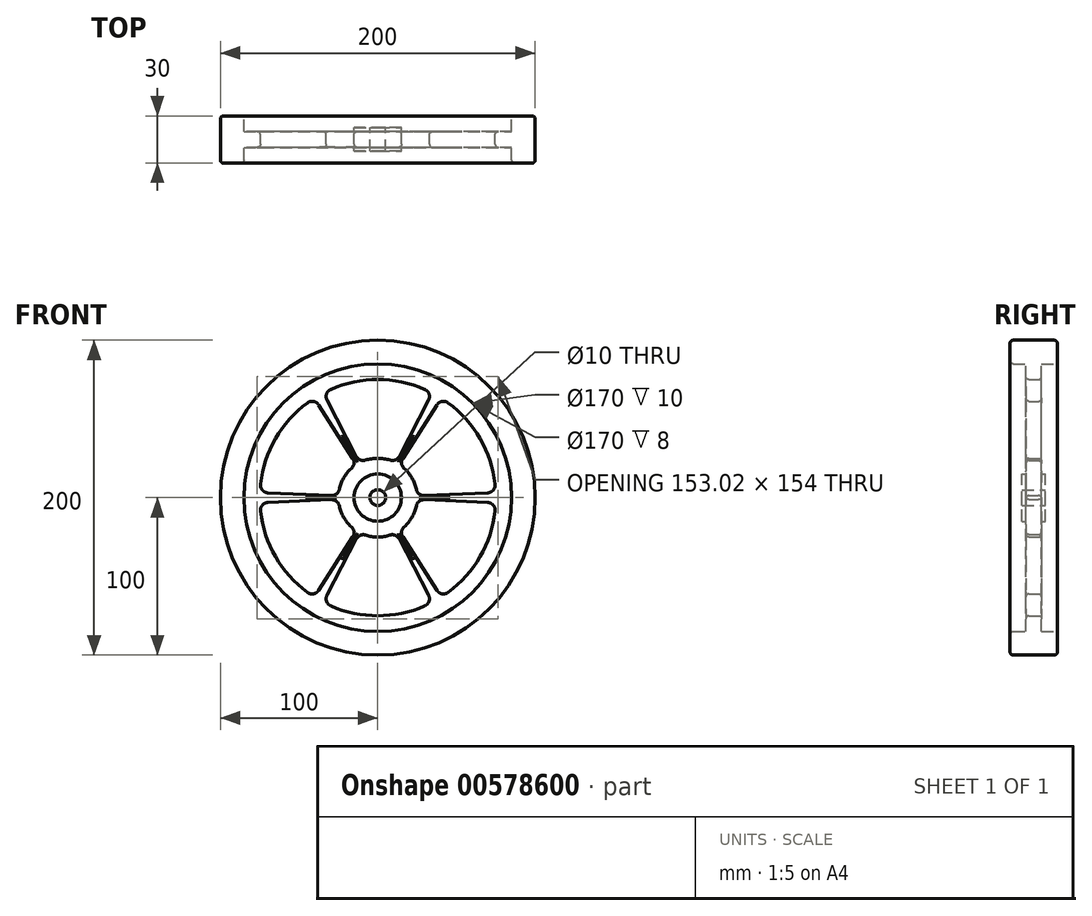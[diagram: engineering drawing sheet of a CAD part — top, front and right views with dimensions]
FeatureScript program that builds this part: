
annotation { "Feature Type Name" : "Feature", "Feature Type Description" : "" }
export const myFeature = defineFeature(function(context is Context, id is Id, definition is map)
    precondition{}
    {
        {
            var Q0;
            Q0=qCreatedBy(makeId("Front.planeOp"),FACE);
            var sketch = newSketch(context, id + "F0", { "sketchPlane" : qUnion([Q0])});
            skCircle(sketch, "E0", {"center": v(0, 0) * mm, "radius": 100 * mm});
            skCircle(sketch, "E1.0", {"center": v(0, 0) * mm, "radius": 85 * mm});
            skCircle(sketch, "E2", {"center": v(0, 0) * mm, "radius": 5 * mm});
            skCircle(sketch, "E3.0", {"center": v(0, 0) * mm, "radius": 15 * mm});
            skArc(sketch, "E4.0", {"start": v(-7.69, -23.79) * mm, "mid": v(0, -25) * mm, "end": v(7.69, -23.79) * mm});
            skArc(sketch, "E5.0", {"start": v(-29.8, -68.83) * mm, "mid": v(0, -75) * mm, "end": v(29.8, -68.83) * mm});
            skLineSegment(sketch, "E6", {"start": v(0, 0) * mm, "end": v(0, -117.3) * mm, "construction": true});
            skLineSegment(sketch, "E7", {"start": v(13.66, -26.24) * mm, "end": v(32.24, -61.93) * mm});
            skLineSegment(sketch, "E8.MirrorCS", {"start": v(-13.66, -26.24) * mm, "end": v(-32.24, -61.93) * mm});
            skPoint(sketch, "E9.visualSharp", {"position": v(34.63, -66.53) * mm});
            skArc(sketch, "E9.filletArc", {"start": v(29.8, -68.83) * mm, "mid": v(32.52, -65.91) * mm, "end": v(32.24, -61.93) * mm});
            skPoint(sketch, "E10.visualSharp", {"position": v(-34.63, -66.53) * mm});
            skArc(sketch, "E10.filletArc", {"start": v(-32.24, -61.93) * mm, "mid": v(-32.52, -65.91) * mm, "end": v(-29.8, -68.83) * mm});
            skPoint(sketch, "E11.visualSharp", {"position": v(-11.54, -22.18) * mm});
            skArc(sketch, "E11.filletArc", {"start": v(-7.69, -23.79) * mm, "mid": v(-11.12, -23.92) * mm, "end": v(-13.66, -26.24) * mm});
            skPoint(sketch, "E12.visualSharp", {"position": v(11.54, -22.18) * mm});
            skArc(sketch, "E12.filletArc", {"start": v(13.66, -26.24) * mm, "mid": v(11.12, -23.92) * mm, "end": v(7.69, -23.79) * mm});
            skLineSegment(sketch, "E13.1.0", {"start": v(29.55, -1.3) * mm, "end": v(69.75, -3.05) * mm});
            skArc(sketch, "E13.1.1", {"start": v(16.76, -18.55) * mm, "mid": v(21.65, -12.5) * mm, "end": v(24.45, -5.24) * mm});
            skArc(sketch, "E13.1.2", {"start": v(16.76, -18.55) * mm, "mid": v(15.16, -21.6) * mm, "end": v(15.9, -24.95) * mm});
            skLineSegment(sketch, "E13.1.3", {"start": v(15.9, -24.95) * mm, "end": v(37.51, -58.89) * mm});
            skArc(sketch, "E13.1.4", {"start": v(29.55, -1.3) * mm, "mid": v(26.28, -2.33) * mm, "end": v(24.45, -5.24) * mm});
            skArc(sketch, "E13.1.5", {"start": v(44.71, -60.21) * mm, "mid": v(64.95, -37.5) * mm, "end": v(74.5, -8.62) * mm});
            skArc(sketch, "E13.1.6", {"start": v(74.5, -8.62) * mm, "mid": v(73.34, -4.8) * mm, "end": v(69.75, -3.05) * mm});
            skArc(sketch, "E13.1.7", {"start": v(37.51, -58.89) * mm, "mid": v(40.82, -61.12) * mm, "end": v(44.71, -60.21) * mm});
            skLineSegment(sketch, "E13.2.0", {"start": v(15.9, 24.95) * mm, "end": v(37.51, 58.89) * mm});
            skArc(sketch, "E13.2.1", {"start": v(24.45, 5.24) * mm, "mid": v(21.65, 12.5) * mm, "end": v(16.76, 18.55) * mm});
            skArc(sketch, "E13.2.2", {"start": v(24.45, 5.24) * mm, "mid": v(26.28, 2.33) * mm, "end": v(29.55, 1.3) * mm});
            skLineSegment(sketch, "E13.2.3", {"start": v(29.55, 1.3) * mm, "end": v(69.75, 3.05) * mm});
            skArc(sketch, "E13.2.4", {"start": v(15.9, 24.95) * mm, "mid": v(15.16, 21.6) * mm, "end": v(16.76, 18.55) * mm});
            skArc(sketch, "E13.2.5", {"start": v(74.5, 8.62) * mm, "mid": v(64.95, 37.5) * mm, "end": v(44.71, 60.21) * mm});
            skArc(sketch, "E13.2.6", {"start": v(44.71, 60.21) * mm, "mid": v(40.82, 61.12) * mm, "end": v(37.51, 58.89) * mm});
            skArc(sketch, "E13.2.7", {"start": v(69.75, 3.05) * mm, "mid": v(73.34, 4.8) * mm, "end": v(74.5, 8.62) * mm});
            skLineSegment(sketch, "E14.2.3.0", {"start": v(-13.66, 26.24) * mm, "end": v(-32.24, 61.93) * mm});
            skArc(sketch, "E14.3.3.0", {"start": v(7.69, 23.79) * mm, "mid": v(0, 25) * mm, "end": v(-7.69, 23.79) * mm});
            skArc(sketch, "E14.7.3.0", {"start": v(7.69, 23.79) * mm, "mid": v(11.12, 23.92) * mm, "end": v(13.66, 26.24) * mm});
            skLineSegment(sketch, "E14.11.3.0", {"start": v(13.66, 26.24) * mm, "end": v(32.24, 61.93) * mm});
            skArc(sketch, "E14.14.3.0", {"start": v(-13.66, 26.24) * mm, "mid": v(-11.12, 23.92) * mm, "end": v(-7.69, 23.79) * mm});
            skArc(sketch, "E14.18.3.0", {"start": v(29.8, 68.83) * mm, "mid": v(0, 75) * mm, "end": v(-29.8, 68.83) * mm});
            skArc(sketch, "E14.22.3.0", {"start": v(-29.8, 68.83) * mm, "mid": v(-32.52, 65.91) * mm, "end": v(-32.24, 61.93) * mm});
            skArc(sketch, "E14.26.3.0", {"start": v(32.24, 61.93) * mm, "mid": v(32.52, 65.91) * mm, "end": v(29.8, 68.83) * mm});
            skLineSegment(sketch, "E14.2.4.0", {"start": v(-29.55, 1.3) * mm, "end": v(-69.75, 3.05) * mm});
            skArc(sketch, "E14.3.4.0", {"start": v(-16.76, 18.55) * mm, "mid": v(-21.65, 12.5) * mm, "end": v(-24.45, 5.24) * mm});
            skArc(sketch, "E14.7.4.0", {"start": v(-16.76, 18.55) * mm, "mid": v(-15.16, 21.6) * mm, "end": v(-15.9, 24.95) * mm});
            skLineSegment(sketch, "E14.11.4.0", {"start": v(-15.9, 24.95) * mm, "end": v(-37.51, 58.89) * mm});
            skArc(sketch, "E14.14.4.0", {"start": v(-29.55, 1.3) * mm, "mid": v(-26.28, 2.33) * mm, "end": v(-24.45, 5.24) * mm});
            skArc(sketch, "E14.18.4.0", {"start": v(-44.71, 60.21) * mm, "mid": v(-64.95, 37.5) * mm, "end": v(-74.5, 8.62) * mm});
            skArc(sketch, "E14.22.4.0", {"start": v(-74.5, 8.62) * mm, "mid": v(-73.34, 4.8) * mm, "end": v(-69.75, 3.05) * mm});
            skArc(sketch, "E14.26.4.0", {"start": v(-37.51, 58.89) * mm, "mid": v(-40.82, 61.12) * mm, "end": v(-44.71, 60.21) * mm});
            skLineSegment(sketch, "E14.2.5.0", {"start": v(-15.9, -24.95) * mm, "end": v(-37.51, -58.89) * mm});
            skArc(sketch, "E14.3.5.0", {"start": v(-24.45, -5.24) * mm, "mid": v(-21.65, -12.5) * mm, "end": v(-16.76, -18.55) * mm});
            skArc(sketch, "E14.7.5.0", {"start": v(-24.45, -5.24) * mm, "mid": v(-26.28, -2.33) * mm, "end": v(-29.55, -1.3) * mm});
            skLineSegment(sketch, "E14.11.5.0", {"start": v(-29.55, -1.3) * mm, "end": v(-69.75, -3.05) * mm});
            skArc(sketch, "E14.14.5.0", {"start": v(-15.9, -24.95) * mm, "mid": v(-15.16, -21.6) * mm, "end": v(-16.76, -18.55) * mm});
            skArc(sketch, "E14.18.5.0", {"start": v(-74.5, -8.62) * mm, "mid": v(-64.95, -37.5) * mm, "end": v(-44.71, -60.21) * mm});
            skArc(sketch, "E14.22.5.0", {"start": v(-44.71, -60.21) * mm, "mid": v(-40.82, -61.12) * mm, "end": v(-37.51, -58.89) * mm});
            skArc(sketch, "E14.26.5.0", {"start": v(-69.75, -3.05) * mm, "mid": v(-73.34, -4.8) * mm, "end": v(-74.5, -8.62) * mm});
            skSolve(sketch);
        }
        {
            var Q0;
            Q0=makeQuery(id+"F0.imprint","IMPRINT",FACE,{"disambiguationData":[TD([[makeQuery(id+"F0.imprint","IMPRINT",EDGE,{"derivedFrom":sQuery(id+"F0.wireOp",EDGE,"E2")}),-1.0]])]});
            extrude(context, id + "F1", {"entities" : qUnion([Q0]), "endBound" : BoundingType.SYMMETRIC, "depth" : 15 * mm, "offsetDistance" : 25 * mm});
        }
        {
            var Q0;
            Q0=makeQuery(id+"F0.imprint","IMPRINT",FACE,{"disambiguationData":[TD([[makeQuery(id+"F0.imprint","IMPRINT",EDGE,{"derivedFrom":sQuery(id+"F0.wireOp",EDGE,"E1.0")}),1.0]])]});
            extrude(context, id + "F2", {"entities" : qUnion([Q0]), "operationType" : NewBodyOperationType.ADD, "endBound" : BoundingType.SYMMETRIC, "depth" : 10 * mm, "offsetDistance" : 25 * mm});
        }
        {
            var Q0;
            Q0=makeQuery(id+"F0.imprint","IMPRINT",FACE,{"disambiguationData":[TD([[makeQuery(id+"F0.imprint","IMPRINT",EDGE,{"derivedFrom":sQuery(id+"F0.wireOp",EDGE,"E0")}),1.0]])]});
            extrude(context, id + "F3", {"entities" : qUnion([Q0]), "operationType" : NewBodyOperationType.ADD, "endBound" : BoundingType.SYMMETRIC, "depth" : 30 * mm, "offsetDistance" : 25 * mm});
        }
        {
            var Q0;
            Q0=makeQuery(id+"F3.opExtrude","CAP_EDGE",EDGE,{"disambiguationData":[OSD([sQuery(id+"F0.wireOp",EDGE,"E0")])],"isStart":false});
            var Q1;
            Q1=makeQuery(id+"F3.opExtrude","CAP_EDGE",EDGE,{"disambiguationData":[OSD([sQuery(id+"F0.wireOp",EDGE,"E0")])],"isStart":true});
            var Q2;
            Q2=makeQuery(id+"F3.opExtrude","CAP_EDGE",EDGE,{"disambiguationData":[OSD([sQuery(id+"F0.wireOp",EDGE,"E1.0")])],"isStart":false});
            var Q3;
            Q3=makeQuery(id+"F2.opExtrude","CAP_EDGE",EDGE,{"disambiguationData":[OSD([sQuery(id+"F0.wireOp",EDGE,"E1.0")])],"isStart":false});
            var Q4;
            Q4=makeQuery(id+"F2.opExtrude","CAP_EDGE",EDGE,{"disambiguationData":[OSD([sQuery(id+"F0.wireOp",EDGE,"E14.18.5.0")])],"isStart":false});
            var Q5;
            Q5=makeQuery(id+"F2.opExtrude","CAP_EDGE",EDGE,{"disambiguationData":[OSD([sQuery(id+"F0.wireOp",EDGE,"E5.0")])],"isStart":false});
            var Q6;
            Q6=makeQuery(id+"F2.opExtrude","CAP_EDGE",EDGE,{"disambiguationData":[OSD([sQuery(id+"F0.wireOp",EDGE,"E13.1.5")])],"isStart":false});
            var Q7;
            Q7=makeQuery(id+"F2.opExtrude","CAP_EDGE",EDGE,{"disambiguationData":[OSD([sQuery(id+"F0.wireOp",EDGE,"E13.2.3")])],"isStart":false});
            var Q8;
            Q8=makeQuery(id+"F2.opExtrude","CAP_EDGE",EDGE,{"disambiguationData":[OSD([sQuery(id+"F0.wireOp",EDGE,"E14.11.3.0")])],"isStart":false});
            var Q9;
            Q9=makeQuery(id+"F2.opExtrude","CAP_EDGE",EDGE,{"disambiguationData":[OSD([sQuery(id+"F0.wireOp",EDGE,"E14.11.4.0")])],"isStart":false});
            var Q10;
            Q10=makeQuery(id+"F2.opExtrude","CAP_EDGE",EDGE,{"disambiguationData":[OSD([sQuery(id+"F0.wireOp",EDGE,"E14.11.5.0")])],"isStart":true});
            var Q11;
            Q11=makeQuery(id+"F2.opExtrude","CAP_EDGE",EDGE,{"disambiguationData":[OSD([sQuery(id+"F0.wireOp",EDGE,"E14.18.4.0")])],"isStart":true});
            var Q12;
            Q12=makeQuery(id+"F2.opExtrude","CAP_EDGE",EDGE,{"disambiguationData":[OSD([sQuery(id+"F0.wireOp",EDGE,"E14.18.3.0")])],"isStart":true});
            var Q13;
            Q13=makeQuery(id+"F2.opExtrude","CAP_EDGE",EDGE,{"disambiguationData":[OSD([sQuery(id+"F0.wireOp",EDGE,"E13.2.5")])],"isStart":true});
            var Q14;
            Q14=makeQuery(id+"F2.opExtrude","CAP_EDGE",EDGE,{"disambiguationData":[OSD([sQuery(id+"F0.wireOp",EDGE,"E13.1.0")])],"isStart":true});
            var Q15;
            Q15=makeQuery(id+"F2.opExtrude","CAP_EDGE",EDGE,{"disambiguationData":[OSD([sQuery(id+"F0.wireOp",EDGE,"E7")])],"isStart":true});
            fillet(context, id + "F4", {"entities" : qUnion([Q0, Q1, Q2, Q3, Q4, Q5, Q6, Q7, Q8, Q9, Q10, Q11, Q12, Q13, Q14, Q15]), "radius" : 2 * mm, "tangentPropagation" : true, "allowEdgeOverflow" : false});
        }
        {
            var Q0;
            Q0=qCreatedBy(makeId("Right.planeOp"),FACE);
            var sketch = newSketch(context, id + "F5", { "sketchPlane" : qUnion([Q0])});
            skLineSegment(sketch, "E15", {"start": v(-0.31, 12.22) * mm, "end": v(-129.93, 12.22) * mm, "construction": true});
            skLineSegment(sketch, "E16", {"start": v(-122.76, 12.22) * mm, "end": v(-122.76, 27.22) * mm});
            skLineSegment(sketch, "E17", {"start": v(-122.76, 27.22) * mm, "end": v(-22.76, 27.22) * mm});
            skLineSegment(sketch, "E18", {"start": v(-22.76, 27.22) * mm, "end": v(-22.76, 17.22) * mm});
            skLineSegment(sketch, "E19", {"start": v(-22.76, 17.22) * mm, "end": v(-2.76, 17.22) * mm});
            skLineSegment(sketch, "E20", {"start": v(-2.76, 17.22) * mm, "end": v(-2.76, 12.22) * mm});
            skSolve(sketch);
        }
        {
            var Q0;
            Q0=sQuery(id+"F5.wireOp",EDGE,"E18");
            var Q1;
            Q1=sQuery(id+"F5.wireOp",EDGE,"E17");
            var Q2;
            Q2=sQuery(id+"F5.wireOp",EDGE,"E19");
            var Q3;
            Q3=sQuery(id+"F5.wireOp",EDGE,"E20");
            var Q4;
            Q4=sQuery(id+"F5.wireOp",EDGE,"E16");
            var Q5;
            Q5=sQuery(id+"F5.wireOp",EDGE,"E15");
            revolve(context, id + "F6", {"bodyType" : ToolBodyType.SURFACE, "surfaceEntities" : qUnion([Q0, Q1, Q2, Q3, Q4]), "axis" : qUnion([Q5]), "revolveType" : RevolveType.FULL});
        }
        {
            var Q0;
            Q0=makeQuery(id+"F6.opRevolve","SWEPT_EDGE",EDGE,{"disambiguationData":[OSD([sQuery(id+"F5.wireOp",VERTEX,"E17.end")])]});
            var Q1;
            Q1=makeQuery(id+"F6.opRevolve","SWEPT_EDGE",EDGE,{"disambiguationData":[OSD([sQuery(id+"F5.wireOp",VERTEX,"E16.end")])]});
            chamfer(context, id + "F7", {"entities" : qUnion([Q0, Q1]), "width" : 5 * mm, "tangentPropagation" : true});
        }
    });
